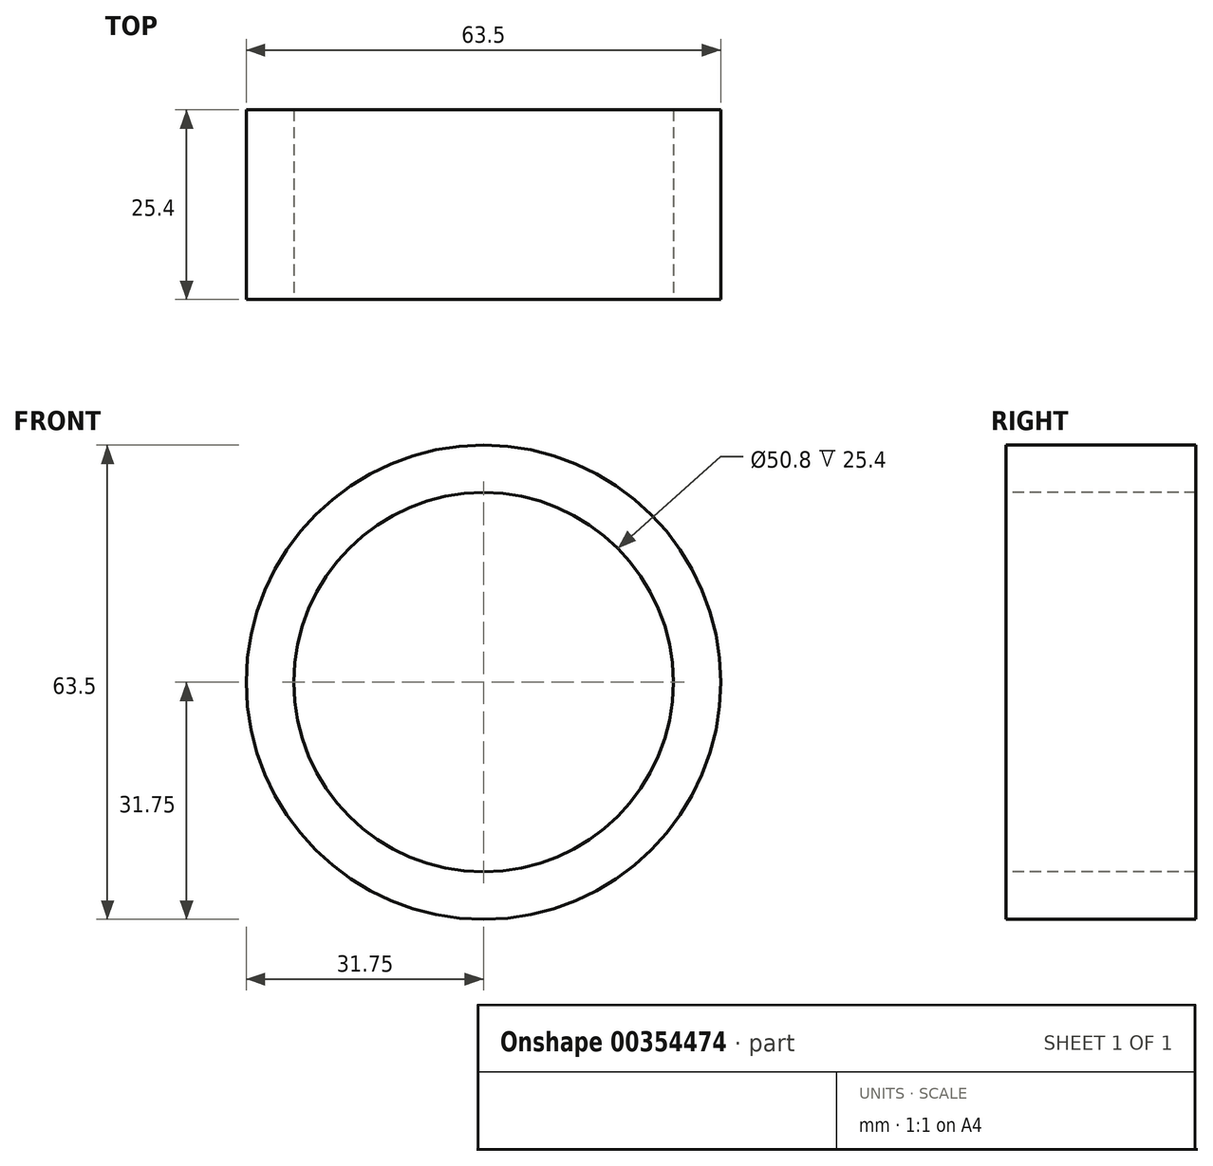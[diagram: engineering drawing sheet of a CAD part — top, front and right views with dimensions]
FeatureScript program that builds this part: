
annotation { "Feature Type Name" : "Feature", "Feature Type Description" : "" }
export const myFeature = defineFeature(function(context is Context, id is Id, definition is map)
    precondition{}
    {
        {
            var Q0;
            Q0=qCreatedBy(makeId("Front.planeOp"),FACE);
            var sketch = newSketch(context, id + "F0", { "sketchPlane" : qUnion([Q0])});
            skCircle(sketch, "E0", {"center": v(0, 0) * mm, "radius": 25.4 * mm});
            skCircle(sketch, "E1", {"center": v(0, 0) * mm, "radius": 31.75 * mm});
            skSolve(sketch);
        }
        {
            var Q0;
            Q0=makeQuery(id+"F0.imprint","IMPRINT",FACE,{"disambiguationData":[TD([[makeQuery(id+"F0.imprint","IMPRINT",EDGE,{"derivedFrom":sQuery(id+"F0.wireOp",EDGE,"E0")}),-1.0]])]});
            extrude(context, id + "F1", {"entities" : qUnion([Q0]), "oppositeDirection" : true, "depth" : 25.4 * mm});
        }
    });
